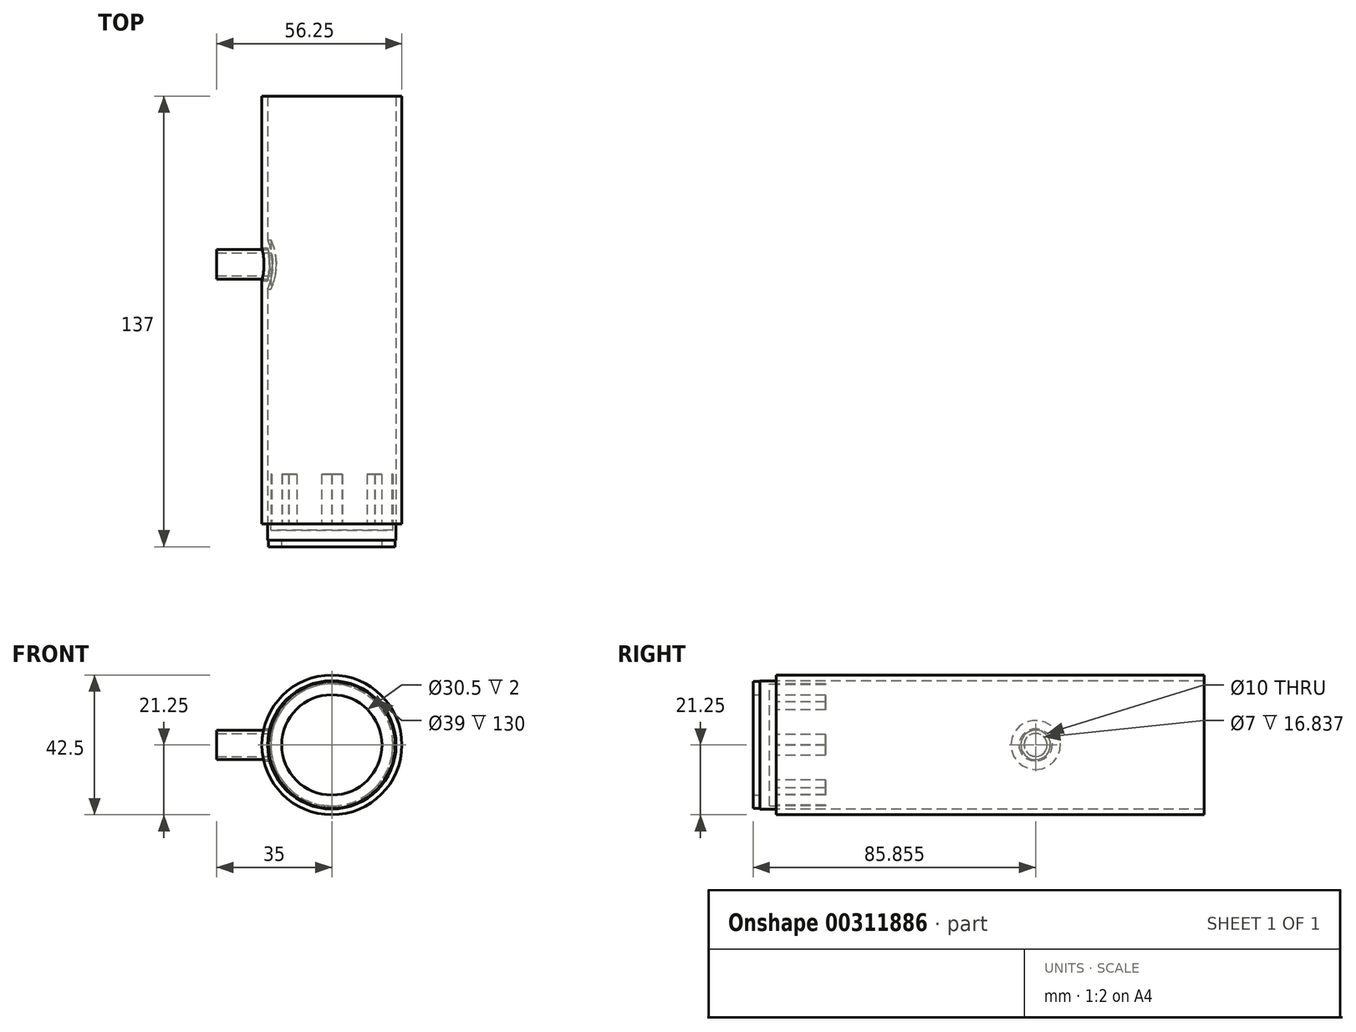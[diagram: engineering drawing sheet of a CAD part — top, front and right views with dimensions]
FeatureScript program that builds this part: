
annotation { "Feature Type Name" : "Feature", "Feature Type Description" : "" }
export const myFeature = defineFeature(function(context is Context, id is Id, definition is map)
    precondition{}
    {
        {
            var Q0;
            Q0=qCreatedBy(makeId("Front.planeOp"),FACE);
            var sketch = newSketch(context, id + "F0", { "sketchPlane" : qUnion([Q0])});
            skCircle(sketch, "E0", {"center": v(0, 0) * mm, "radius": 19.5 * mm});
            skCircle(sketch, "E1", {"center": v(0, 0) * mm, "radius": 21.25 * mm});
            skSolve(sketch);
        }
        {
            var Q0;
            Q0 = qSketchRegion(id + "F0", true);
            extrude(context, id + "F1", {"entities" : qUnion([Q0]), "oppositeDirection" : true, "depth" : 130 * mm});
        }
        {
            var Q0;
            Q0=qCreatedBy(makeId("Front.planeOp"),FACE);
            var sketch = newSketch(context, id + "F2", { "sketchPlane" : qUnion([Q0])});
            skCircle(sketch, "E2", {"center": v(0, 0) * mm, "radius": 18.55 * mm});
            skSolve(sketch);
        }
        {
            var Q0;
            Q0 = qSketchRegion(id + "F2", true);
            extrude(context, id + "F3", {"entities" : qUnion([Q0]), "depth" : 2 * mm});
        }
        {
            var Q0;
            Q0=qCreatedBy(makeId("Right.planeOp"),FACE);
            var sketch = newSketch(context, id + "F4", { "sketchPlane" : qUnion([Q0])});
            skLineSegment(sketch, "E3", {"start": v(0, 0) * mm, "end": v(11.34, 0) * mm, "construction": true});
            skSolve(sketch);
        }
        {
            var Q0;
            Q0=makeQuery(id+"F3.opExtrude","CAP_FACE",FACE,{"disambiguationData":[OSD([sQuery(id+"F2.wireOp",EDGE,"E2")])],"isStart":true});
            var sketch = newSketch(context, id + "F5", { "sketchPlane" : qUnion([Q0])});
            skCircle(sketch, "E4", {"center": v(0, 0) * mm, "radius": 4 * mm});
            skArc(sketch, "E5", {"start": v(0, 4) * mm, "mid": v(1.22, 11.77) * mm, "end": v(-3.18, 18.28) * mm});
            skArc(sketch, "E6", {"start": v(1.38, 3.76) * mm, "mid": v(3.58, 11.42) * mm, "end": v(0, 18.55) * mm});
            skSolve(sketch);
        }
        {
            var Q0;
            {var subQ0=sQuery(id+"F5.wireOp",EDGE,"E5");Q0=makeQuery(id+"F5.imprint","IMPRINT",FACE,{"disambiguationData":[TD([[makeQuery(id+"F5.imprint","IMPRINT",EDGE,{"derivedFrom":subQ0}),-1.0]])]});}
            extrude(context, id + "F6", {"entities" : qUnion([Q0]), "operationType" : NewBodyOperationType.ADD, "depth" : 15 * mm});
        }
        {
            var Q0;
            Q0=makeQuery(id+"F3.opExtrude","SWEPT_BODY",BODY,{"disambiguationData":[OSD([sQuery(id+"F2.wireOp",EDGE,"E2")])]});
            var Q1;
            Q1=sQuery(id+"F4.wireOp",EDGE,"E3");
            circularPattern(context, id + "F7", {"entities" : qUnion([Q0]), "axis" : qUnion([Q1]), "angle" : 360 * degree, "instanceCount" : 8, "equalSpace" : true});
        }
        {
            var Q0;
            Q0=makeQuery(id+"F7.opPattern","COPY",FACE,{"derivedFrom":makeQuery(id+"F3.opExtrude","CAP_FACE",FACE,{"disambiguationData":[OSD([sQuery(id+"F2.wireOp",EDGE,"E2")])],"isStart":true}),"instanceName":"1"});
            var sketch = newSketch(context, id + "F8", { "sketchPlane" : qUnion([Q0])});
            skCircle(sketch, "E7", {"center": v(0, 0) * mm, "radius": 4.5 * mm});
            skCircle(sketch, "E8", {"center": v(0, 0) * mm, "radius": 1 * mm});
            skSolve(sketch);
        }
        {
            var Q0;
            Q0 = qSketchRegion(id + "F8", true);
            extrude(context, id + "F9", {"entities" : qUnion([Q0]), "operationType" : NewBodyOperationType.ADD, "depth" : 25 * mm});
        }
        {
            var Q0;
            Q0=makeQuery(id+"F9.opExtrude","CAP_FACE",FACE,{"disambiguationData":[OSD([sQuery(id+"F8.wireOp",EDGE,"E7"),sQuery(id+"F8.wireOp",EDGE,"E8")])],"isStart":false});
            cPlane(context, id + "F10", {"entities" : qUnion([Q0]), "cplaneType" : CPlaneType.OFFSET, "offset" : 1 * mm, "width" : 150 * mm, "height" : 150 * mm});
        }
        {
            var Q0;
            Q0=qCreatedBy(id+"F10.planeOp",FACE);
            var sketch = newSketch(context, id + "F11", { "sketchPlane" : qUnion([Q0])});
            skCircle(sketch, "E9", {"center": v(0, 0) * mm, "radius": 1 * mm});
            skSolve(sketch);
        }
        {
            var Q0;
            Q0 = qSketchRegion(id + "F11", true);
            extrude(context, id + "F12", {"entities" : qUnion([Q0]), "depth" : 10 * mm});
        }
        {
            var Q0;
            Q0=makeQuery(id+"F12.opExtrude","CAP_FACE",FACE,{"disambiguationData":[OSD([sQuery(id+"F11.wireOp",EDGE,"E9")])],"isStart":false});
            var sketch = newSketch(context, id + "F13", { "sketchPlane" : qUnion([Q0])});
            skCircle(sketch, "E10", {"center": v(0, 0) * mm, "radius": 1.61 * mm});
            skSolve(sketch);
        }
        {
            var Q0;
            Q0 = qSketchRegion(id + "F13", true);
            extrude(context, id + "F14", {"entities" : qUnion([Q0]), "operationType" : NewBodyOperationType.ADD, "depth" : 5 * mm});
        }
        {
            var Q0;
            Q0=makeQuery(id+"F14.opExtrude","CAP_FACE",FACE,{"disambiguationData":[OSD([sQuery(id+"F13.wireOp",EDGE,"E10")])],"isStart":false});
            var sketch = newSketch(context, id + "F15", { "sketchPlane" : qUnion([Q0])});
            skCircle(sketch, "E11", {"center": v(0, 0) * mm, "radius": 10 * mm});
            skSolve(sketch);
        }
        {
            var Q0;
            Q0 = qSketchRegion(id + "F15", true);
            extrude(context, id + "F16", {"entities" : qUnion([Q0]), "operationType" : NewBodyOperationType.ADD, "depth" : 15 * mm});
        }
        {
            var Q0;
            {var subQ0=sQuery(id+"F2.wireOp",EDGE,"E2");Q0=makeQuery(id+"F9.boolean.opBoolean","SPLIT",FACE,{"disambiguationData":[TD([makeQuery(id+"F6.opExtrude","SWEPT_FACE",FACE,{"disambiguationData":[OSD([sQuery(id+"F5.wireOp",EDGE,"E5")])]})])],"derivedFrom":makeQuery(id+"F3.opExtrude","CAP_FACE",FACE,{"disambiguationData":[OSD([subQ0])],"isStart":true})});}
            cPlane(context, id + "F17", {"entities" : qUnion([Q0]), "cplaneType" : CPlaneType.OFFSET, "offset" : 30 * mm, "width" : 150 * mm, "height" : 150 * mm});
        }
        {
            var Q0;
            Q0=qCreatedBy(id+"F17.planeOp",FACE);
            var sketch = newSketch(context, id + "F18", { "sketchPlane" : qUnion([Q0])});
            skCircle(sketch, "E12", {"center": v(0, 0) * mm, "radius": 13.5 * mm});
            skCircle(sketch, "E13", {"center": v(0, 0) * mm, "radius": 5 * mm});
            skCircle(sketch, "E14", {"center": v(0, 8) * mm, "radius": 1 * mm});
            skCircle(sketch, "E15", {"center": v(0, -8) * mm, "radius": 1 * mm});
            skSolve(sketch);
        }
        {
            var Q0;
            Q0 = qSketchRegion(id + "F18", true);
            extrude(context, id + "F19", {"entities" : qUnion([Q0]), "depth" : 2 * mm});
        }
        {
            var Q0;
            Q0=makeQuery(id+"F19.opExtrude","CAP_FACE",FACE,{"disambiguationData":[OSD([sQuery(id+"F18.wireOp",EDGE,"E12"),sQuery(id+"F18.wireOp",EDGE,"E13"),sQuery(id+"F18.wireOp",EDGE,"E14"),sQuery(id+"F18.wireOp",EDGE,"E15")])],"isStart":false});
            var sketch = newSketch(context, id + "F20", { "sketchPlane" : qUnion([Q0])});
            skCircle(sketch, "E16", {"center": v(0, 0) * mm, "radius": 13.5 * mm});
            skCircle(sketch, "E17", {"center": v(0, 0) * mm, "radius": 15 * mm});
            skCircle(sketch, "E18", {"center": v(0, 0) * mm, "radius": 16 * mm});
            skSolve(sketch);
        }
        {
            var Q0;
            Q0 = qSketchRegion(id + "F20", true);
            extrude(context, id + "F21", {"entities" : qUnion([Q0]), "operationType" : NewBodyOperationType.ADD, "depth" : 25 * mm});
        }
        {
            var Q0;
            Q0=makeQuery(id+"F1.opExtrude","CAP_FACE",FACE,{"disambiguationData":[OSD([sQuery(id+"F0.wireOp",EDGE,"E0"),sQuery(id+"F0.wireOp",EDGE,"E1")])],"isStart":true});
            var sketch = newSketch(context, id + "F22", { "sketchPlane" : qUnion([Q0])});
            skCircle(sketch, "E19", {"center": v(0, 0) * mm, "radius": 19.5 * mm});
            skSolve(sketch);
        }
        {
            var Q0;
            Q0 = qSketchRegion(id + "F22", true);
            extrude(context, id + "F23", {"entities" : qUnion([Q0]), "depth" : 5 * mm});
        }
        {
            var Q0;
            Q0=makeQuery(id+"F1.opExtrude","CAP_FACE",FACE,{"disambiguationData":[OSD([sQuery(id+"F0.wireOp",EDGE,"E0"),sQuery(id+"F0.wireOp",EDGE,"E1")])],"isStart":true});
            var sketch = newSketch(context, id + "F24", { "sketchPlane" : qUnion([Q0])});
            skCircle(sketch, "E20", {"center": v(0, 0) * mm, "radius": 19.25 * mm});
            skCircle(sketch, "E21", {"center": v(-8, 0) * mm, "radius": 2 * mm});
            skCircle(sketch, "E22", {"center": v(8, 0) * mm, "radius": 2 * mm});
            skCircle(sketch, "E23", {"center": v(0, 0) * mm, "radius": 5.25 * mm});
            skLineSegment(sketch, "E24", {"start": v(-8, 0) * mm, "end": v(8, 0) * mm, "construction": true});
            skSolve(sketch);
        }
        {
            var Q0;
            Q0 = qSketchRegion(id + "F24", true);
            extrude(context, id + "F25", {"entities" : qUnion([Q0]), "depth" : 3 * mm});
        }
        {
            var Q0;
            Q0=makeQuery(id+"F25.opExtrude","CAP_FACE",FACE,{"disambiguationData":[OSD([sQuery(id+"F24.wireOp",EDGE,"E20"),sQuery(id+"F24.wireOp",EDGE,"E21"),sQuery(id+"F24.wireOp",EDGE,"E22"),sQuery(id+"F24.wireOp",EDGE,"E23")])],"isStart":false});
            var sketch = newSketch(context, id + "F26", { "sketchPlane" : qUnion([Q0])});
            skCircle(sketch, "E25", {"center": v(0, 0) * mm, "radius": 15.25 * mm});
            skCircle(sketch, "E26", {"center": v(0, 0) * mm, "radius": 19.25 * mm});
            skSolve(sketch);
        }
        {
            var Q0;
            Q0 = qSketchRegion(id + "F26", true);
            extrude(context, id + "F27", {"entities" : qUnion([Q0]), "operationType" : NewBodyOperationType.ADD, "depth" : 4 * mm});
        }
        {
            var Q0;
            Q0=qCreatedBy(makeId("Right.planeOp"),FACE);
            var sketch = newSketch(context, id + "F28", { "sketchPlane" : qUnion([Q0])});
            skLineSegment(sketch, "E27", {"start": v(0, 0) * mm, "end": v(109.18, 0) * mm, "construction": true});
            skCircle(sketch, "E28", {"center": v(78.86, 0) * mm, "radius": 5 * mm});
            skSolve(sketch);
        }
        {
            var Q0;
            Q0 = qSketchRegion(id + "F28", true);
            extrude(context, id + "F29", {"entities" : qUnion([Q0]), "operationType" : NewBodyOperationType.REMOVE, "oppositeDirection" : true, "depth" : 25 * mm});
        }
        {
            var Q0;
            Q0=qCreatedBy(makeId("Right.planeOp"),FACE);
            var sketch = newSketch(context, id + "F30", { "sketchPlane" : qUnion([Q0])});
            skCircle(sketch, "E29", {"center": v(78.86, 0) * mm, "radius": 4.5 * mm});
            skCircle(sketch, "E30", {"center": v(78.86, 0) * mm, "radius": 3.5 * mm});
            skSolve(sketch);
        }
        {
            var Q0;
            Q0 = qSketchRegion(id + "F30", true);
            extrude(context, id + "F31", {"entities" : qUnion([Q0]), "oppositeDirection" : true, "depth" : 35 * mm});
        }
        {
            var Q0;
            Q0=qCreatedBy(makeId("Right.planeOp"),FACE);
            var sketch = newSketch(context, id + "F32", { "sketchPlane" : qUnion([Q0])});
            skCircle(sketch, "E31", {"center": v(78.86, 0) * mm, "radius": 7.5 * mm});
            skCircle(sketch, "E32", {"center": v(78.86, 0) * mm, "radius": 4.5 * mm});
            skSolve(sketch);
        }
        {
            var Q0;
            Q0 = qSketchRegion(id + "F32", true);
            var Q1;
            Q1=makeQuery(id+"F1.opExtrude","SWEPT_FACE",FACE,{"disambiguationData":[OSD([sQuery(id+"F0.wireOp",EDGE,"E0")])]});
            extrude(context, id + "F33", {"entities" : qUnion([Q0]), "operationType" : NewBodyOperationType.ADD, "endBound" : BoundingType.UP_TO_SURFACE, "oppositeDirection" : true, "endBoundEntityFace" : qUnion([Q1]), "depth" : 25 * mm});
        }
        {
            var Q0;
            Q0=qCreatedBy(makeId("Front.planeOp"),FACE);
            var sketch = newSketch(context, id + "F34", { "sketchPlane" : qUnion([Q0])});
            skCircle(sketch, "E33", {"center": v(0, 0) * mm, "radius": 18.5 * mm});
            skSolve(sketch);
        }
        {
            var Q0;
            Q0 = qSketchRegion(id + "F34", true);
            extrude(context, id + "F35", {"entities" : qUnion([Q0]), "operationType" : NewBodyOperationType.REMOVE, "oppositeDirection" : true, "depth" : 200 * mm});
        }
    });
